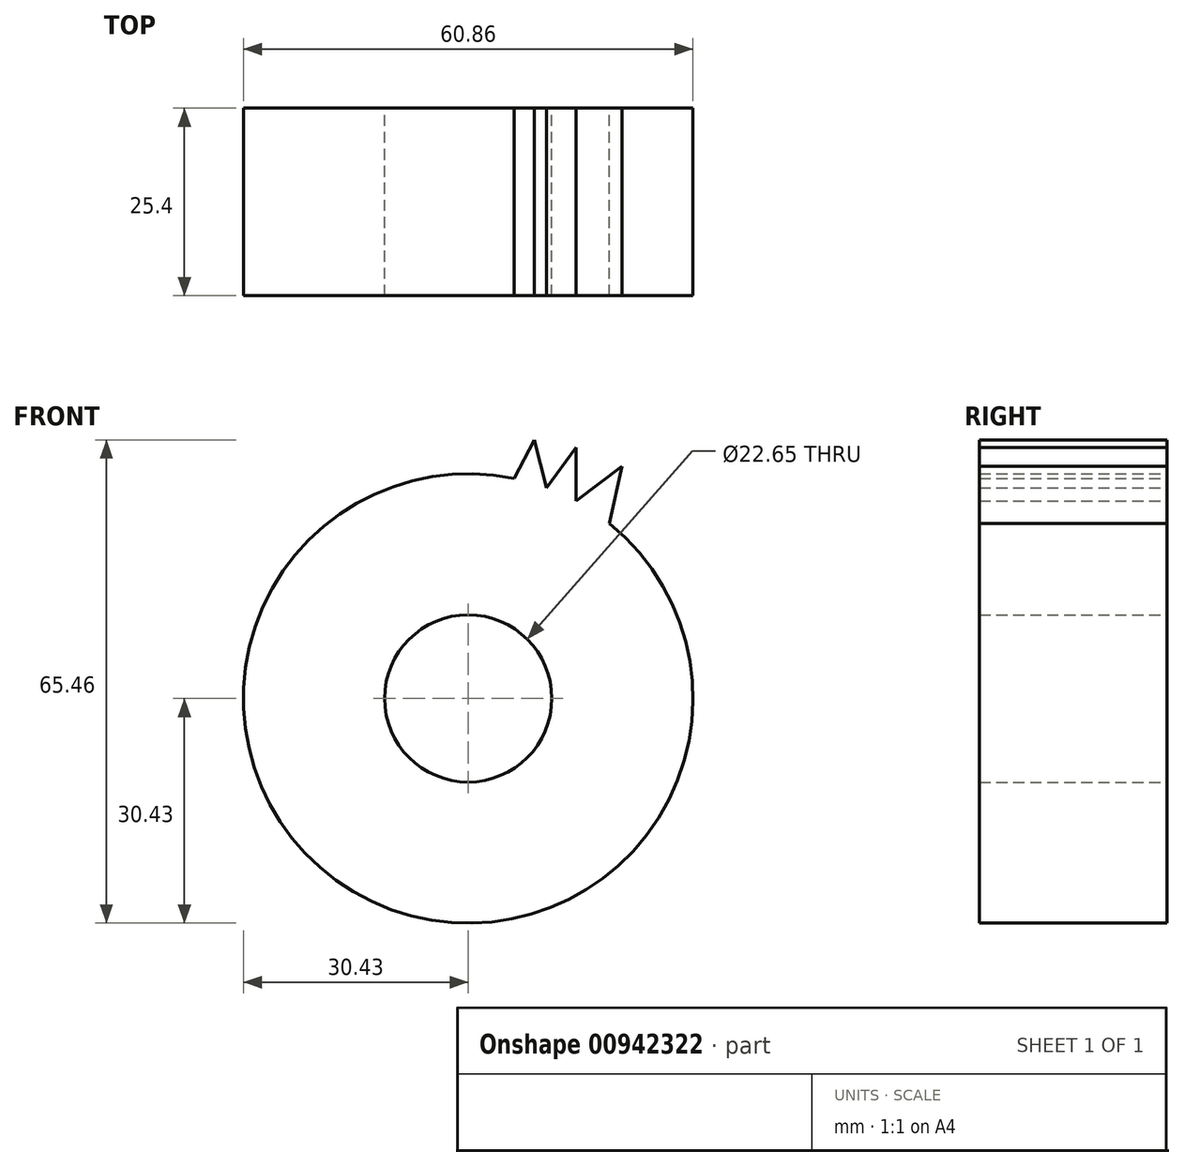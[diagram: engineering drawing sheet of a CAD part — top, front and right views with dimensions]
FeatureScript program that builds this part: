
annotation { "Feature Type Name" : "Feature", "Feature Type Description" : "" }
export const myFeature = defineFeature(function(context is Context, id is Id, definition is map)
    precondition{}
    {
        {
            var Q0;
            Q0=qCreatedBy(makeId("Front.planeOp"),FACE);
            var sketch = newSketch(context, id + "F0", { "sketchPlane" : qUnion([Q0])});
            skCircle(sketch, "E0", {"center": v(0, 0) * mm, "radius": 11.33 * mm});
            skCircle(sketch, "E1", {"center": v(0, 0) * mm, "radius": 30.43 * mm});
            skLineSegment(sketch, "E2", {"start": v(6.25, 29.78) * mm, "end": v(8.96, 35.03) * mm});
            skLineSegment(sketch, "E3", {"start": v(8.96, 35.03) * mm, "end": v(10.6, 28.52) * mm});
            skLineSegment(sketch, "E4", {"start": v(10.6, 28.52) * mm, "end": v(14.57, 33.96) * mm});
            skLineSegment(sketch, "E5", {"start": v(14.57, 33.96) * mm, "end": v(14.57, 26.72) * mm});
            skLineSegment(sketch, "E6", {"start": v(14.57, 26.72) * mm, "end": v(20.85, 31.42) * mm});
            skLineSegment(sketch, "E7", {"start": v(20.85, 31.42) * mm, "end": v(19.1, 23.7) * mm});
            skSolve(sketch);
        }
        {
            var Q0;
            Q0 = qSketchRegion(id + "F0", true);
            extrude(context, id + "F1", {"entities" : qUnion([Q0]), "depth" : 25.4 * mm, "offsetDistance" : 25.4 * mm});
        }
    });
